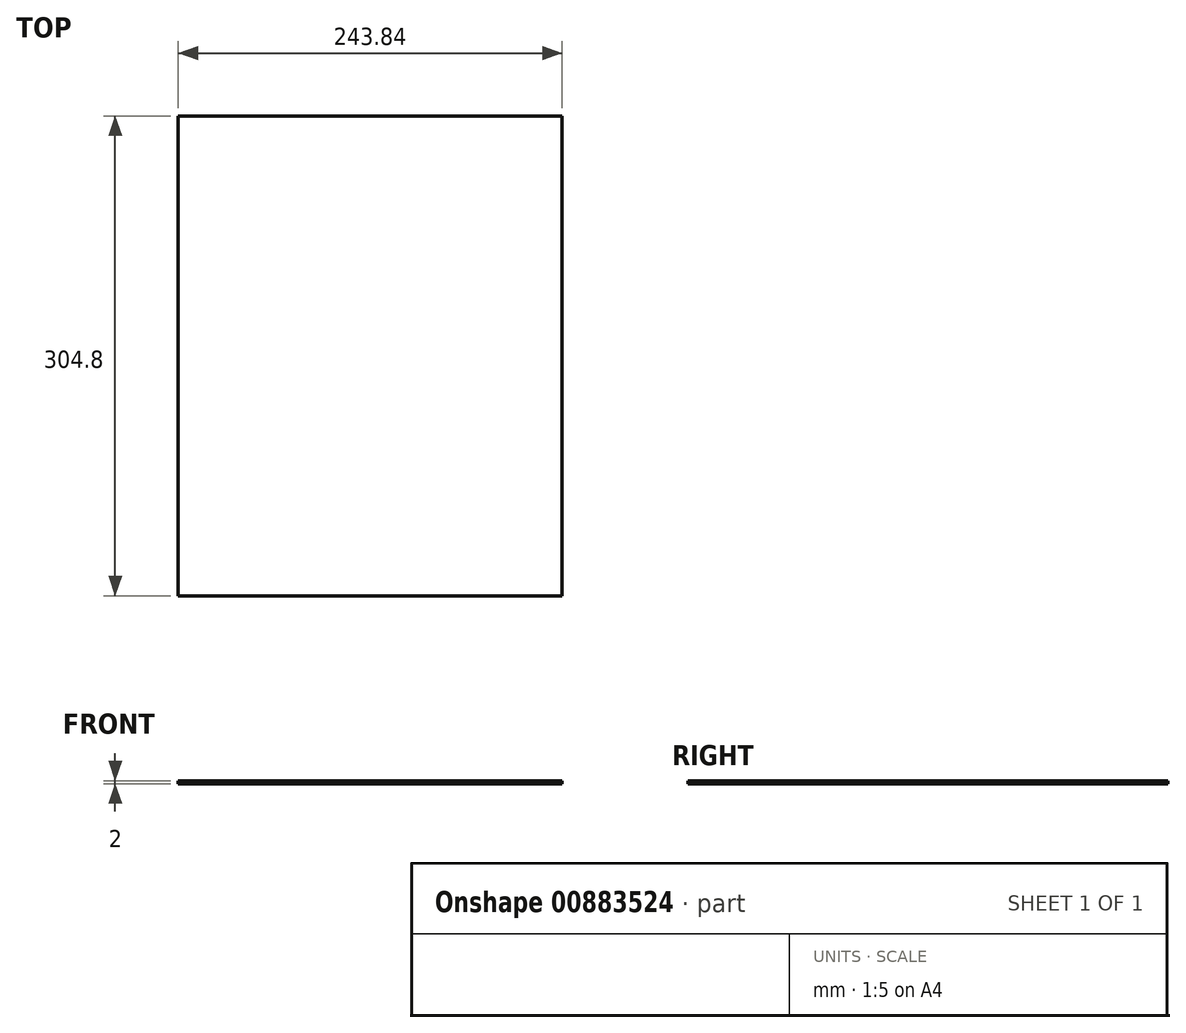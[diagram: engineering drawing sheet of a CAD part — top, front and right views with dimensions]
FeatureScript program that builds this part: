
annotation { "Feature Type Name" : "Feature", "Feature Type Description" : "" }
export const myFeature = defineFeature(function(context is Context, id is Id, definition is map)
    precondition{}
    {
        {
            var Q0;
            Q0=qCreatedBy(makeId("Top.planeOp"),FACE);
            var sketch = newSketch(context, id + "F0", { "sketchPlane" : qUnion([Q0])});
            skLineSegment(sketch, "E0.bottom", {"start": v(-125.24, 0) * mm, "end": v(118.6, 0) * mm});
            skLineSegment(sketch, "E0.top", {"start": v(-125.24, -304.8) * mm, "end": v(118.6, -304.8) * mm});
            skLineSegment(sketch, "E0.left", {"start": v(-125.24, 0) * mm, "end": v(-125.24, -304.8) * mm});
            skLineSegment(sketch, "E0.right", {"start": v(118.6, 0) * mm, "end": v(118.6, -304.8) * mm});
            skSolve(sketch);
        }
        {
            var Q0;
            Q0 = qSketchRegion(id + "F0", true);
            extrude(context, id + "F1", {"entities" : qUnion([Q0]), "oppositeDirection" : true, "depth" : 2 * mm, "offsetDistance" : 25.4 * mm});
        }
    });
